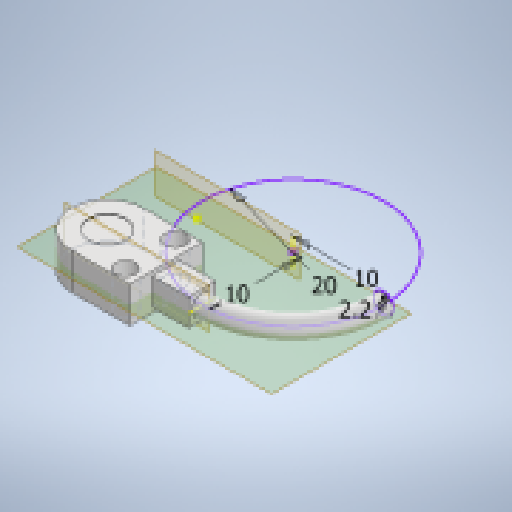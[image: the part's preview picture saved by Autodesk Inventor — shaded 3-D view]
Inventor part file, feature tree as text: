
AUTODESK INVENTOR PART (.ipt)
format: ipt  version: 2023 (Build 270158000, 158)  size: 201,216 bytes
history: native  units: mm
features: sketch x6, extrude x3, plane x3, revolve x1
ambient origin geometry x8: Origin, YZ Plane, XZ Plane, XY Plane, X Axis, Y Axis, Z Axis, Center Point
bodies: Solid1 (feature_tree)
feature tree (13):
  extrude  "Extrusion1"  Depth=8.0mm
  extrude  "Extrusion2"  Depth=5.5mm
  extrude  "Extrusion3"  Depth=1.75mm
  sketch  "Sketch4"  dims[d6=2.2mm d7=2.2mm]
  plane  "Work Plane2"
  sketch  "Sketch5"  dims[d8=4.0mm d9=0.0mm]
  plane  "Work Plane3"
  sketch  "Sketch6"  dims[d10=3.0mm d11=3.0mm d12=0.5mm d13=5.5mm d14=4.0mm d15=0.0mm d16=4.1mm d17=0.1mm d18=0.0mm d19=2.2mm d22=-10.0mm d23=10.0mm d24=2.2mm d25=20.0mm d26=10.0mm d27=90.0deg]
  revolve  "Revolution1"  [1 undecoded]
  sketch  "Sketch1"  dims[d0=8.0mm d1=6.5mm]
  sketch  "Sketch2"  dims[d2=5.5mm d3=2.75mm]
  sketch  "Sketch3"  dims[d4=1.75mm d5=1.75mm]
  plane  "Work Plane1"
note: 1 required parameter value undecoded (feature->parameter linkage not recoverable at this tier; creation-order binding heuristic only, values carry confidence <= 0.55)
